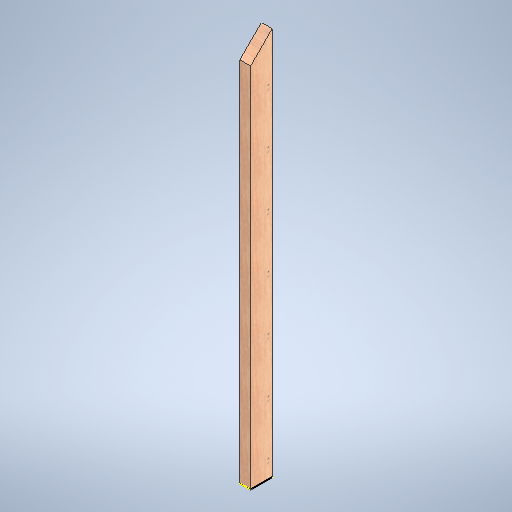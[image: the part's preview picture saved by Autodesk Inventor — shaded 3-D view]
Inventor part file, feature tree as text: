
AUTODESK INVENTOR PART (.ipt)
format: ipt  version: 2025 (Build 290162000, 162)  size: 312,320 bytes
history: native  units: in
note: dims shown in document units (in); Inventor stores cm internally (conversion verified against a paired STEP export)
features: sketch x3, extrude x2
ambient origin geometry x8: Origin, YZ Plane, XZ Plane, XY Plane, X Axis, Y Axis, Z Axis, Center Point
bodies: Solid1 (feature_tree)
feature tree (5):
  extrude  "Extrusion1"  Depth=4.0in
  extrude  "Extrusion2"  TaperAngle=45.0deg  [1 undecoded]
  sketch  "Sketch3"  dims[d5=2.0in d6=0.0in d7=0.5in d8=0.0344in]
  sketch  "Sketch1"  dims[d0=2.0in d1=4.0in]
  sketch  "Sketch2"  dims[d2=72.0in d3=0.0in d4=45.0deg]
note: 1 required parameter value undecoded (feature->parameter linkage not recoverable at this tier; creation-order binding heuristic only, values carry confidence <= 0.55)
